# Revit family: Sanitary_Showers_hansgrohe_27809007-Vernis-Blend-Shower-arm-24-cm__
name_source: partatom
category: Plumbing Fixtures
revit_build: Autodesk Revit 2015 (Build: 20140322_1515(x64)
units: mm (PartAtom-declared; Revit-internal decimal feet)

## types (1)
- Chrome 000
    BIMobject category = Showers
    BIMobject category code = sanitary-showers
    BIMobject main category = Sanitary
    BIMobject main category code = sanitary
    Brand url = http://www.hansgrohe-int.com
    Default Elevation = 1219.2 mm  [stored 4 ft]
    Design country = Germany
    Edition number = 1
    GTIN code = https://4059625282076
    IFC Classification = Sanitary Terminal
    Manufacturer country = Germany
    Manufacturer name = hansgrohe
    Material main = Chrome
    Product Guid = 6be176d2-3282-4fbd-a82b-0cda11afba0d
    Product SKU = 27809007
    Product certification = https://www.hansgrohe.com.cn
    Product data url = https://bimobject.com
    Product family = Shower arms
    Product group = Vernis Blend
    Product name = 27809007 Vernis Blend Shower arm 24 cm
    Product url = https://www.hansgrohe.com.cn
    QR code = http://bimobject.com
    Technical description = https://www.hansgrohe.com.cn

note: [stored X ft] marks values corroborated as IEEE doubles in the binary element streams (Revit-internal decimal feet)

## geometry (parser evidence)
native form markers: Blend x5, Sweep x3
no freeform markers — native parametric forms only
